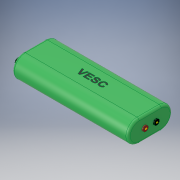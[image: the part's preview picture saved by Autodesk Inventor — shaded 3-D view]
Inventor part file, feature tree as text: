
AUTODESK INVENTOR PART (.ipt)
format: ipt  version: 2019.2 (Build 232265000, 265)  size: 402,944 bytes
history: native  units: mm
features: sketch x9, other x5, extrude x3, fillet x2, emboss x1, chamfer x1
ambient origin geometry x8: Origin, YZ Plane, XZ Plane, XY Plane, X Axis, Y Axis, Z Axis, Center Point
bodies: Solid1 (feature_tree)
feature tree (21):
  extrude  "Extrusion1"  Depth=40.0mm
  emboss  "Emboss1"
  extrude  "Extrusion2"  Depth=2.5mm
  extrude  "Extrusion3"  Depth=0.1mm TaperAngle=0.0deg
  fillet  "Fillet1"  Radius=5.0mm
  fillet  "Fillet2"  Radius=10.0mm
  chamfer  "Chamfer1"  Distance=5.0mm
  sketch  "Sketch5"  dims[d13=5.0mm]
  other  "NEGAITVE"
  sketch  "Sketch6"  dims[d14=5.0mm]
  other  "POSITIVE"
  sketch  "Sketch7"  dims[d15=15.0mm]
  other  "OUT_1"
  sketch  "Sketch8"  dims[d16=15.0mm]
  other  "OUT_2"
  sketch  "Sketch9"  dims[d17=1.0mm d18=0.0mm d19=10.0mm d20=2.0mm d21=0.1mm d22=2.0mm d23=45.0deg]
  other  "OUT_3"
  sketch  "Sketch1"  dims[d0=105.0mm d1=40.0mm]
  sketch  "Sketch2"  dims[d2=20.0mm d3=0.0mm d4=2.5mm]
  sketch  "Sketch3"  dims[d5=2.5mm d6=0.1mm d7=0.0mm d8=5.0mm d9=10.0mm]
  sketch  "Sketch4"  dims[d10=5.0mm d11=5.0mm d12=0.0mm]
